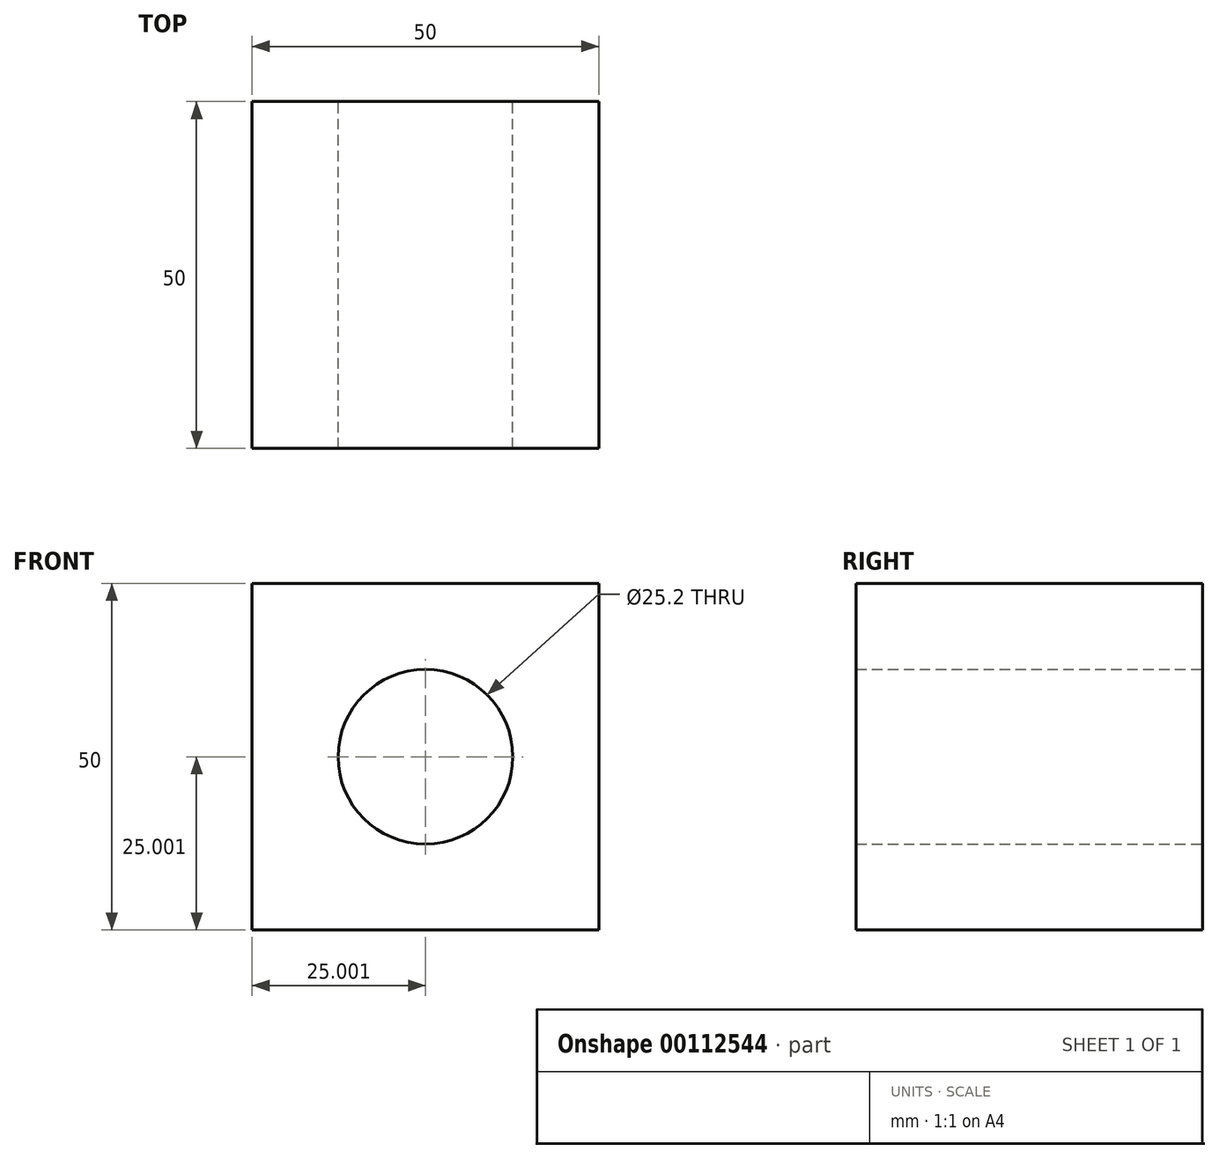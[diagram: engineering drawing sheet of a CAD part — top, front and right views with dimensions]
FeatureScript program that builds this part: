
annotation { "Feature Type Name" : "Feature", "Feature Type Description" : "" }
export const myFeature = defineFeature(function(context is Context, id is Id, definition is map)
    precondition{}
    {
        {
            var Q0;
            Q0=qCreatedBy(makeId("Front.planeOp"),FACE);
            var sketch = newSketch(context, id + "F0", { "sketchPlane" : qUnion([Q0])});
            skLineSegment(sketch, "E0.bottom", {"start": v(-20.5, 24.1) * mm, "end": v(29.5, 24.1) * mm});
            skLineSegment(sketch, "E0.top", {"start": v(-20.5, -25.9) * mm, "end": v(29.5, -25.9) * mm});
            skLineSegment(sketch, "E0.left", {"start": v(-20.5, 24.1) * mm, "end": v(-20.5, -25.9) * mm});
            skLineSegment(sketch, "E0.right", {"start": v(29.5, 24.1) * mm, "end": v(29.5, -25.9) * mm});
            skLineSegment(sketch, "E1", {"start": v(-20.5, 24.1) * mm, "end": v(29.5, -25.9) * mm});
            skLineSegment(sketch, "E2", {"start": v(29.5, 24.1) * mm, "end": v(-20.5, -25.9) * mm});
            skCircle(sketch, "E3", {"center": v(4.5, -0.9) * mm, "radius": 12.6 * mm});
            skSolve(sketch);
        }
        {
            var Q0;
            {var subQ0=sQuery(id+"F0.wireOp",EDGE,"E0.left");Q0=makeQuery(id+"F0.imprint","IMPRINT",FACE,{"disambiguationData":[TD([[makeQuery(id+"F0.imprint","IMPRINT",EDGE,{"derivedFrom":subQ0}),1.0]])]});}
            var Q1;
            {var subQ0=sQuery(id+"F0.wireOp",EDGE,"E0.bottom");Q1=makeQuery(id+"F0.imprint","IMPRINT",FACE,{"disambiguationData":[TD([[makeQuery(id+"F0.imprint","IMPRINT",EDGE,{"derivedFrom":subQ0}),-1.0]])]});}
            var Q2;
            {var subQ0=sQuery(id+"F0.wireOp",EDGE,"E0.top");Q2=makeQuery(id+"F0.imprint","IMPRINT",FACE,{"disambiguationData":[TD([[makeQuery(id+"F0.imprint","IMPRINT",EDGE,{"derivedFrom":subQ0}),1.0]])]});}
            var Q3;
            {var subQ0=sQuery(id+"F0.wireOp",EDGE,"E0.right");Q3=makeQuery(id+"F0.imprint","IMPRINT",FACE,{"disambiguationData":[TD([[makeQuery(id+"F0.imprint","IMPRINT",EDGE,{"derivedFrom":subQ0}),-1.0]])]});}
            extrude(context, id + "F1", {"entities" : qUnion([Q0, Q1, Q2, Q3]), "depth" : 50 * mm});
        }
    });
